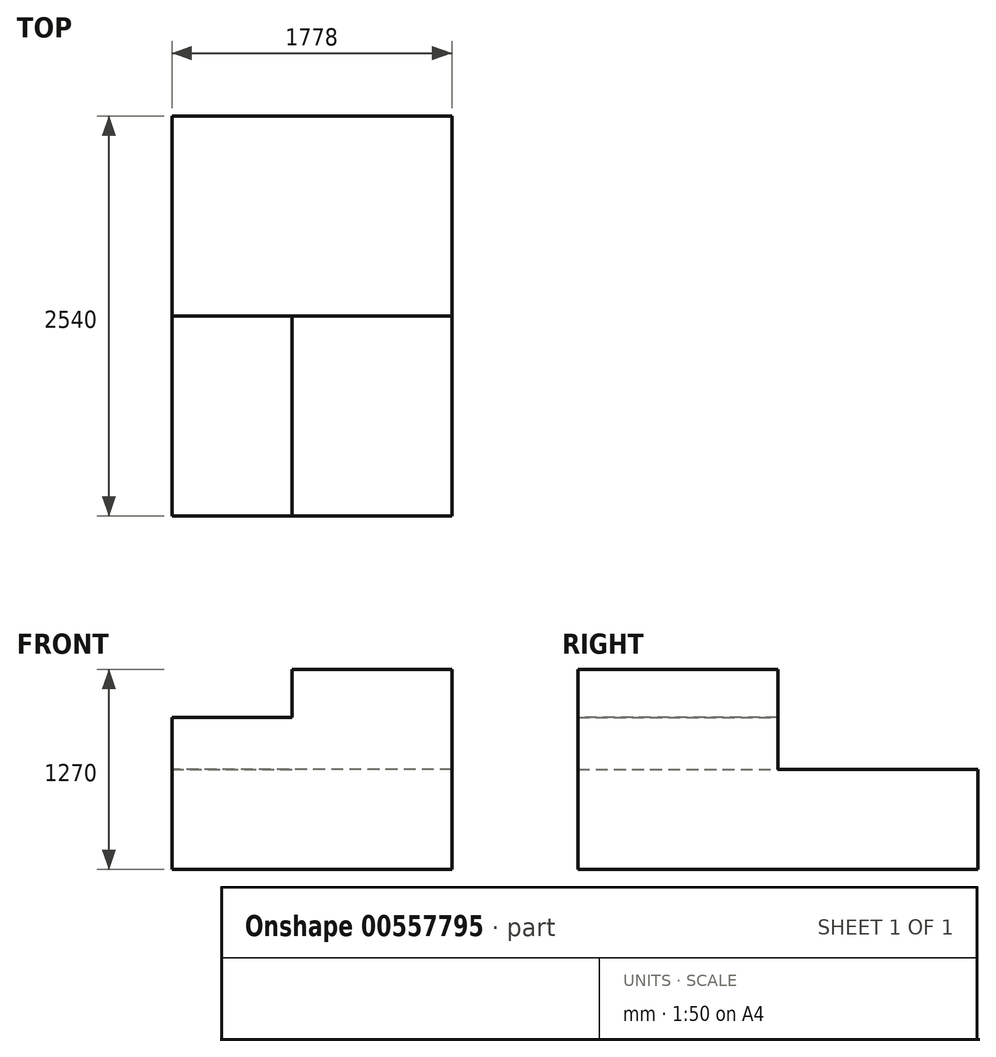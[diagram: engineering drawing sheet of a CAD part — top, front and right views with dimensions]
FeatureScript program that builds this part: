
annotation { "Feature Type Name" : "Feature", "Feature Type Description" : "" }
export const myFeature = defineFeature(function(context is Context, id is Id, definition is map)
    precondition{}
    {
        {
            var Q0;
            Q0=qCreatedBy(makeId("Top.planeOp"),FACE);
            var sketch = newSketch(context, id + "F0", { "sketchPlane" : qUnion([Q0])});
            skLineSegment(sketch, "E0", {"start": v(-763.25, 2531.9) * mm, "end": v(-763.25, -8.1) * mm});
            skLineSegment(sketch, "E1", {"start": v(-763.25, -8.1) * mm, "end": v(1014.75, -8.1) * mm});
            skLineSegment(sketch, "E2", {"start": v(1014.75, -8.1) * mm, "end": v(1014.75, 2531.9) * mm});
            skLineSegment(sketch, "E3", {"start": v(1014.75, 2531.9) * mm, "end": v(-763.25, 2531.9) * mm});
            skSolve(sketch);
        }
        {
            var Q0;
            Q0=makeQuery(id+"F0.imprint","IMPRINT",FACE,{"disambiguationData":[TD([[makeQuery(id+"F0.imprint","IMPRINT",EDGE,{"derivedFrom":sQuery(id+"F0.wireOp",EDGE,"E0")}),1.0]])]});
            extrude(context, id + "F1", {"entities" : qUnion([Q0]), "depth" : 635 * mm, "offsetDistance" : 25.4 * mm});
        }
        {
            var Q0;
            Q0=makeQuery(id+"F1.opExtrude","CAP_FACE",FACE,{"disambiguationData":[OSD([sQuery(id+"F0.wireOp",EDGE,"E0"),sQuery(id+"F0.wireOp",EDGE,"E1"),sQuery(id+"F0.wireOp",EDGE,"E2"),sQuery(id+"F0.wireOp",EDGE,"E3")])],"isStart":false});
            var sketch = newSketch(context, id + "F2", { "sketchPlane" : qUnion([Q0])});
            skLineSegment(sketch, "E4", {"start": v(1014.75, -8.1) * mm, "end": v(1014.75, 1261.9) * mm});
            skLineSegment(sketch, "E5", {"start": v(1014.75, 1261.9) * mm, "end": v(-1.25, 1261.9) * mm});
            skLineSegment(sketch, "E6", {"start": v(-1.25, 1261.9) * mm, "end": v(0, -8.1) * mm});
            skLineSegment(sketch, "E7", {"start": v(0, -8.1) * mm, "end": v(1016, -8.1) * mm});
            skSolve(sketch);
        }
        {
            var Q0;
            {var subQ0=sQuery(id+"F2.wireOp",EDGE,"E4");Q0=makeQuery(id+"F2.imprint","IMPRINT",FACE,{"disambiguationData":[TD([[makeQuery(id+"F2.imprint","IMPRINT",EDGE,{"derivedFrom":subQ0}),1.0]])]});}
            extrude(context, id + "F3", {"entities" : qUnion([Q0]), "operationType" : NewBodyOperationType.ADD, "depth" : 635 * mm, "offsetDistance" : 25.4 * mm});
        }
        {
            var Q0;
            Q0=makeQuery(id+"F1.opExtrude","CAP_FACE",FACE,{"disambiguationData":[OSD([sQuery(id+"F0.wireOp",EDGE,"E0"),sQuery(id+"F0.wireOp",EDGE,"E1"),sQuery(id+"F0.wireOp",EDGE,"E2"),sQuery(id+"F0.wireOp",EDGE,"E3")])],"isStart":false});
            var sketch = newSketch(context, id + "F4", { "sketchPlane" : qUnion([Q0])});
            skLineSegment(sketch, "E8", {"start": v(0, -8.1) * mm, "end": v(-762, -8.1) * mm});
            skLineSegment(sketch, "E9", {"start": v(-762, -8.1) * mm, "end": v(-763.25, 1261.9) * mm});
            skLineSegment(sketch, "E10", {"start": v(-763.25, 1261.9) * mm, "end": v(-1.25, 1261.9) * mm});
            skLineSegment(sketch, "E11", {"start": v(-1.25, 1261.9) * mm, "end": v(0, -8.1) * mm});
            skSolve(sketch);
        }
        {
            var Q0;
            Q0=makeQuery(id+"F4.imprint","IMPRINT",FACE,{"disambiguationData":[TD([[makeQuery(id+"F4.imprint","IMPRINT",EDGE,{"derivedFrom":sQuery(id+"F4.wireOp",EDGE,"E8")}),1.0]])]});
            extrude(context, id + "F5", {"entities" : qUnion([Q0]), "operationType" : NewBodyOperationType.ADD, "depth" : 330.2 * mm, "offsetDistance" : 25.4 * mm});
        }
    });
